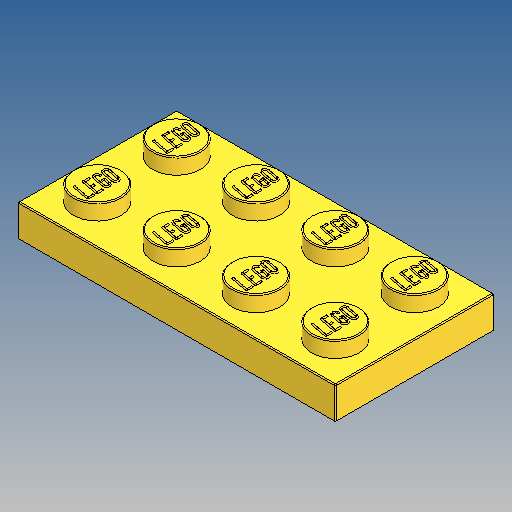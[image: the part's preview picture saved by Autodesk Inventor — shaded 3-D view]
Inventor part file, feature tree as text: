
AUTODESK INVENTOR PART (.ipt)
format: ipt  version: 2025 (Build 290162010, 162A)  size: 5,249,536 bytes
history: native  units: in
note: dims shown in document units (in); Inventor stores cm internally (conversion verified against a paired STEP export)
features: extrude x4, sketch x4, fillet x2, pattern_linear x2, other x1
ambient origin geometry x8: Origin, YZ Plane, XZ Plane, XY Plane, X Axis, Y Axis, Z Axis, Center Point
bodies: Solid1 (feature_tree)
feature tree (13):
  extrude  "Extrusion1"  Depth=0.6299in
  extrude  "Extrusion4"  Depth=0.063in
  other  "LEGO:1"
  fillet  "Fillet2"  Radius=0.063in
  pattern_linear  "Rectangular Pattern1"  Spacing1=0.189in  [1 undecoded]
  sketch  "Sketch3"  dims[d4=0.126in d5=0.0in d7=0.0591in d8=0.063in d11=0.063in d12=0.0in]
  extrude  "Extrusion2"  Depth=0.063in
  extrude  "Extrusion5"  Depth=0.189in
  pattern_linear  "Rectangular Pattern2"  Spacing1=0.1575in  [1 undecoded]
  fillet  "Fillet1"  Radius=0.1575in
  sketch  "Sketch2"  dims[d0=1.2598in d1=0.6299in]
  sketch  "Sketch9"  dims[d22=0.0039in]
  sketch  "Sketch10"  dims[d60=0.2564in d61=0.189in d62=0.063in d63=0.189in d64=0.1575in d65=0.1575in d66=0.063in d67=0.0in d68=0.0039in d69=1.5748in d71=0.315in d72=0.7874in d74=0.315in d75=0.315in d76=0.315in d77=0.0709in d78=0.0in d79=1.1811in d81=0.315in d82=0.3937in d84=0.315in d85=0.0in d86=0.0in d87=0.0in d88=0.0in d89=0.0in d90=0.0in d91=0.0in d92=0.0079in d93=0.0732in d94=0.0281in d95=0.035in d96=0.0079in d97=0.0139in d98=0.0281in d99=0.035in d100=0.0281in d101=0.0159in d102=0.0177in d103=0.035in d104=0.5428in]
note: 2 required parameter values undecoded (feature->parameter linkage not recoverable at this tier; creation-order binding heuristic only, values carry confidence <= 0.55)
